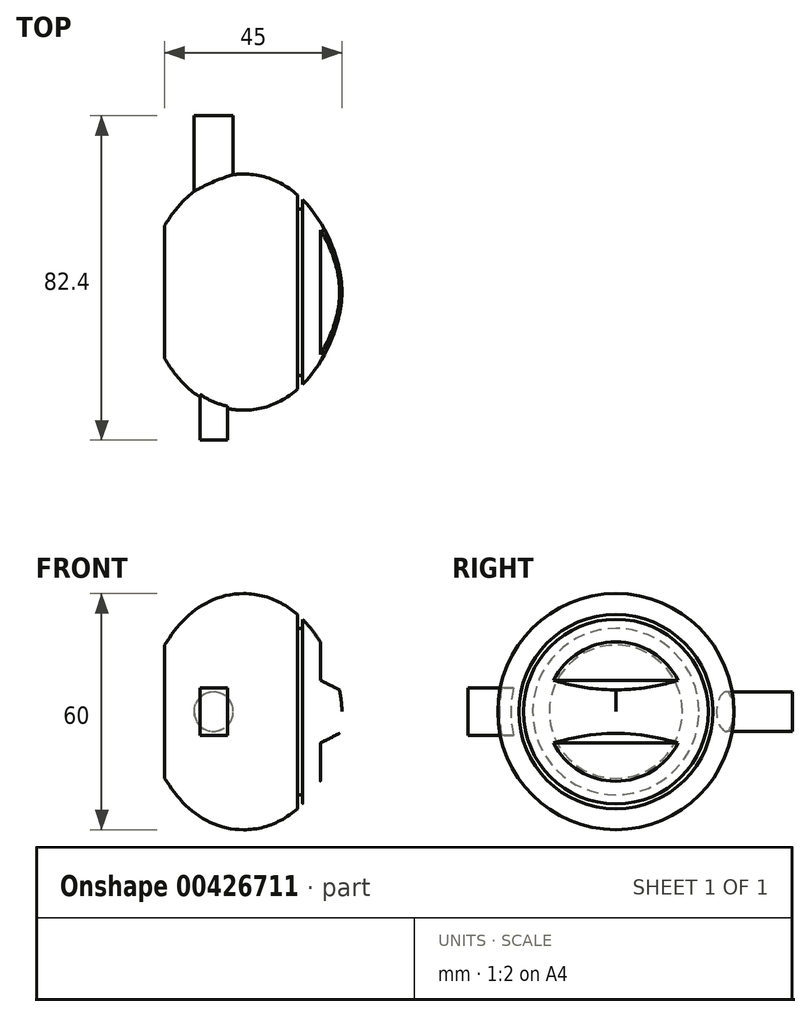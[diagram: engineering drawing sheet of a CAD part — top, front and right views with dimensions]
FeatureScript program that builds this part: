
annotation { "Feature Type Name" : "Feature", "Feature Type Description" : "" }
export const myFeature = defineFeature(function(context is Context, id is Id, definition is map)
    precondition{}
    {
        {
            var Q0;
            Q0=qCreatedBy(makeId("Front.planeOp"),FACE);
            var sketch = newSketch(context, id + "F0", { "sketchPlane" : qUnion([Q0])});
            skLineSegment(sketch, "E0", {"start": v(0, 0) * mm, "end": v(0, 30) * mm, "construction": true});
            skLineSegment(sketch, "E1", {"start": v(0, 0) * mm, "end": v(25, 0) * mm, "construction": true});
            skFitSpline(sketch, "E2", {"points": [v(0, 30) * mm, v(25, 0) * mm], "startDerivative": vector(48.78, 0) * mm, "endDerivative": vector(0, -32.98) * mm});
            skFitSpline(sketch, "E3.MirrorCS", {"points": [v(0, 30) * mm, v(-25, 0) * mm], "startDerivative": vector(-48.78, 0) * mm, "endDerivative": vector(0, -32.98) * mm});
            skLineSegment(sketch, "E4", {"start": v(-20, 16.91) * mm, "end": v(-20, 0) * mm});
            skLineSegment(sketch, "E5", {"start": v(-20, 0) * mm, "end": v(25, 0) * mm});
            skSolve(sketch);
        }
        {
            var Q0;
            Q0 = qSketchRegion(id + "F0", true);
            var Q1;
            Q1 = qConstructionFilter(qBodyType(qCreatedBy(id + "F0" ,EDGE), BodyType.WIRE), ConstructionObject.NO);
            var Q2;
            Q2=sQuery(id+"F0.wireOp",EDGE,"E1");
            revolve(context, id + "F1", {"entities" : qUnion([Q0]), "surfaceEntities" : qUnion([Q1]), "axis" : qUnion([Q2]), "revolveType" : RevolveType.FULL});
        }
        {
            var Q0;
            Q0=qCreatedBy(makeId("Front.planeOp"),FACE);
            var sketch = newSketch(context, id + "F2", { "sketchPlane" : qUnion([Q0])});
            skLineSegment(sketch, "E6", {"start": v(15.64, 0) * mm, "end": v(11.1, 0) * mm, "construction": true});
            skLineSegment(sketch, "E7", {"start": v(19.53, 19.2) * mm, "end": v(19.53, 7.97) * mm});
            skLineSegment(sketch, "E8", {"start": v(19.53, 7.97) * mm, "end": v(26.41, 4.52) * mm});
            skLineSegment(sketch, "E9", {"start": v(26.41, 4.52) * mm, "end": v(26.41, 18.83) * mm});
            skLineSegment(sketch, "E10", {"start": v(26.41, 18.83) * mm, "end": v(19.53, 19.2) * mm});
            skLineSegment(sketch, "E11.MirrorCS", {"start": v(19.53, -19.2) * mm, "end": v(19.53, -7.97) * mm});
            skLineSegment(sketch, "E12.MirrorCS", {"start": v(26.41, -4.52) * mm, "end": v(26.41, -18.83) * mm});
            skLineSegment(sketch, "E13.MirrorCS", {"start": v(19.53, -7.97) * mm, "end": v(26.41, -4.52) * mm});
            skLineSegment(sketch, "E14.MirrorCS", {"start": v(26.41, -18.83) * mm, "end": v(19.53, -19.2) * mm});
            skSolve(sketch);
        }
        {
            var Q0;
            Q0 = qSketchRegion(id + "F2", true);
            extrude(context, id + "F3", {"entities" : qUnion([Q0]), "operationType" : NewBodyOperationType.REMOVE, "endBound" : BoundingType.SYMMETRIC, "oppositeDirection" : true, "depth" : 40 * mm});
        }
        {
            var Q0;
            Q0=qCreatedBy(makeId("Front.planeOp"),FACE);
            var sketch = newSketch(context, id + "F4", { "sketchPlane" : qUnion([Q0])});
            skLineSegment(sketch, "E15.bottom", {"start": v(13.7, 31.41) * mm, "end": v(15, 31.41) * mm});
            skLineSegment(sketch, "E15.top", {"start": v(13.7, 21.13) * mm, "end": v(15, 21.13) * mm});
            skLineSegment(sketch, "E15.left", {"start": v(13.7, 31.41) * mm, "end": v(13.7, 21.13) * mm});
            skLineSegment(sketch, "E15.right", {"start": v(15, 31.41) * mm, "end": v(15, 21.13) * mm});
            skLineSegment(sketch, "E16", {"start": v(3.97, 0) * mm, "end": v(11.65, 0) * mm, "construction": true});
            skSolve(sketch);
        }
        {
            var Q0;
            Q0=makeQuery(id+"F4.imprint","IMPRINT",FACE,{"disambiguationData":[TD([[makeQuery(id+"F4.imprint","IMPRINT",EDGE,{"derivedFrom":sQuery(id+"F4.wireOp",EDGE,"E15.bottom")}),-1.0]])]});
            var Q1;
            Q1=sQuery(id+"F4.wireOp",EDGE,"E16");
            var Q2;
            Q2=sQuery(id+"F4.wireOp",EDGE,"E16");
            revolve(context, id + "F5", {"operationType" : NewBodyOperationType.REMOVE, "entities" : qUnion([Q0]), "surfaceEntities" : qUnion([Q1]), "axis" : qUnion([Q2]), "revolveType" : RevolveType.FULL, "oppositeDirection" : true});
        }
        {
            var Q0;
            Q0=qCreatedBy(makeId("Front.planeOp"),FACE);
            var sketch = newSketch(context, id + "F6", { "sketchPlane" : qUnion([Q0])});
            skLineSegment(sketch, "E17.bottom", {"start": v(-11, 6) * mm, "end": v(-4, 6) * mm});
            skLineSegment(sketch, "E17.top", {"start": v(-11, -6) * mm, "end": v(-4, -6) * mm});
            skLineSegment(sketch, "E17.left", {"start": v(-11, 6) * mm, "end": v(-11, -6) * mm});
            skLineSegment(sketch, "E17.right", {"start": v(-4, 6) * mm, "end": v(-4, -6) * mm});
            skLineSegment(sketch, "E18", {"start": v(-11, 6) * mm, "end": v(-11, 28.39) * mm, "construction": true});
            skSolve(sketch);
        }
        {
            var Q0;
            Q0 = qSketchRegion(id + "F6", true);
            extrude(context, id + "F7", {"entities" : qUnion([Q0]), "operationType" : NewBodyOperationType.ADD, "depth" : 37.6 * mm});
        }
        {
            var Q0;
            Q0=qCreatedBy(makeId("Front.planeOp"),FACE);
            var sketch = newSketch(context, id + "F8", { "sketchPlane" : qUnion([Q0])});
            skCircle(sketch, "E19", {"center": v(-7.6, 0) * mm, "radius": 5 * mm});
            skSolve(sketch);
        }
        {
            var Q0;
            Q0 = qSketchRegion(id + "F8", true);
            extrude(context, id + "F9", {"entities" : qUnion([Q0]), "operationType" : NewBodyOperationType.ADD, "oppositeDirection" : true, "depth" : 44.8 * mm});
        }
    });
